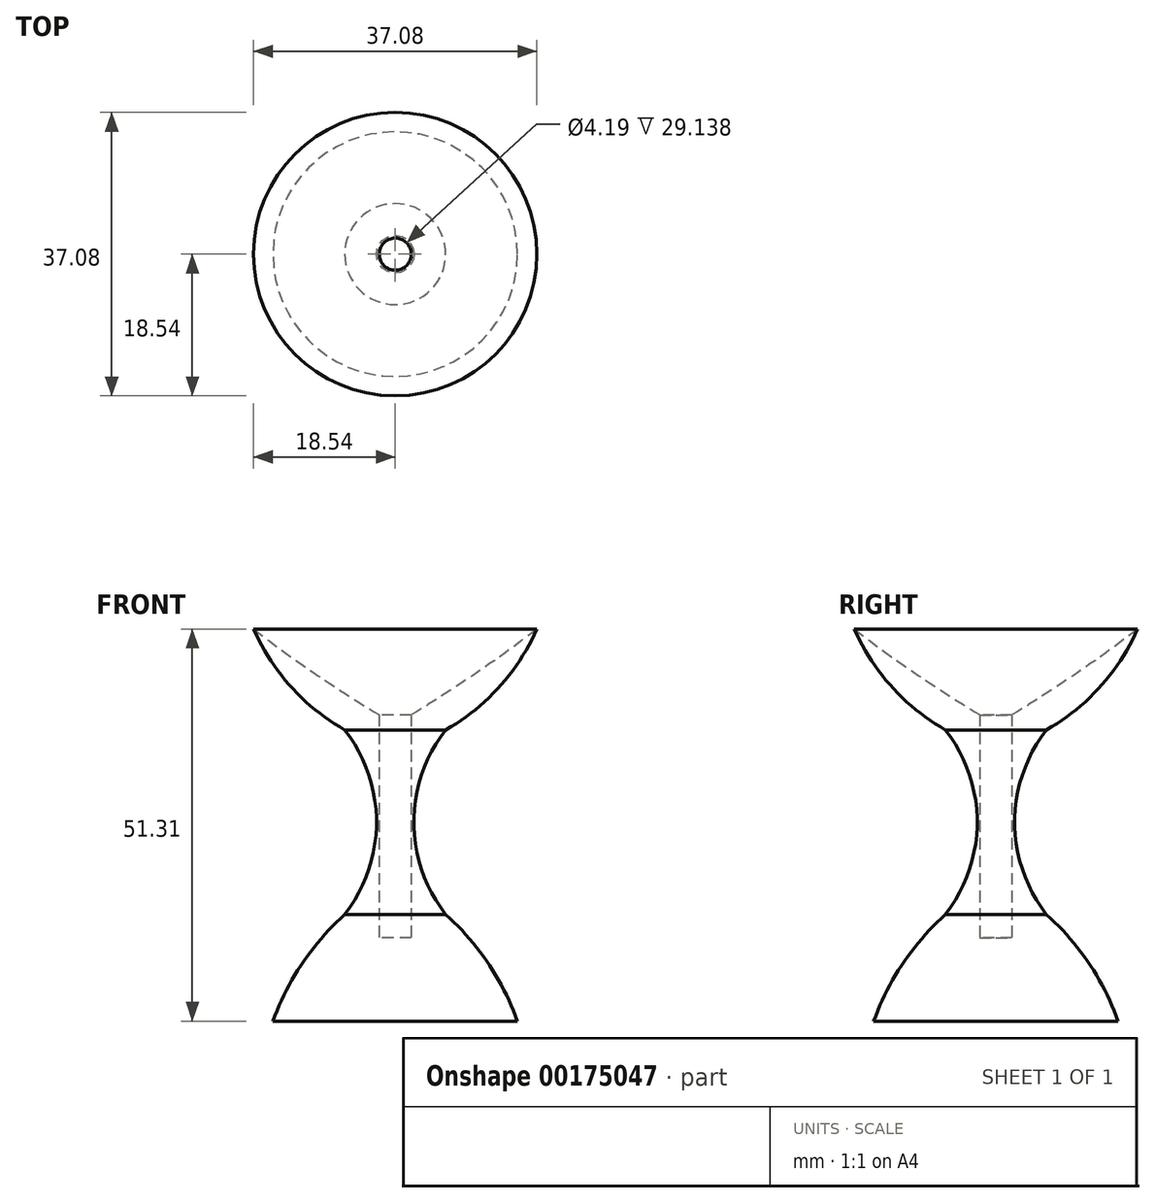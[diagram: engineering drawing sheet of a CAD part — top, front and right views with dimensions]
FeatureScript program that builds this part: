
annotation { "Feature Type Name" : "Feature", "Feature Type Description" : "" }
export const myFeature = defineFeature(function(context is Context, id is Id, definition is map)
    precondition{}
    {
        {
            var Q0;
            Q0=qCreatedBy(makeId("Front.planeOp"),FACE);
            var sketch = newSketch(context, id + "F0", { "sketchPlane" : qUnion([Q0])});
            skLineSegment(sketch, "E0", {"start": v(0, 53.09) * mm, "end": v(0, -54.61) * mm});
            skArc(sketch, "E1", {"start": v(-18.54, 40.39) * mm, "mid": v(-13.64, 32.82) * mm, "end": v(-6.6, 27.18) * mm});
            skArc(sketch, "E2", {"start": v(-6.6, 3.05) * mm, "mid": v(-2.46, 15.11) * mm, "end": v(-6.6, 27.18) * mm});
            skArc(sketch, "E3", {"start": v(-6.6, 3.05) * mm, "mid": v(-12.16, -3.36) * mm, "end": v(-16, -10.92) * mm});
            skLineSegment(sketch, "E4", {"start": v(-16, -10.92) * mm, "end": v(0, -10.92) * mm});
            skArc(sketch, "E5", {"start": v(-18.54, 40.39) * mm, "mid": v(-9.47, 33.85) * mm, "end": v(0, 27.89) * mm});
            skSolve(sketch);
        }
        {
            var Q0;
            Q0 = qSketchRegion(id + "F0", true);
            var Q1;
            Q1=sQuery(id+"F0.wireOp",EDGE,"E0");
            revolve(context, id + "F1", {"entities" : qUnion([Q0]), "axis" : qUnion([Q1]), "revolveType" : RevolveType.FULL});
        }
        {
            var Q0;
            Q0=qCreatedBy(makeId("Top.planeOp"),FACE);
            var sketch = newSketch(context, id + "F2", { "sketchPlane" : qUnion([Q0])});
            skCircle(sketch, "E6", {"center": v(0, 0) * mm, "radius": 2.1 * mm});
            skSolve(sketch);
        }
        {
            var Q0;
            Q0 = qSketchRegion(id + "F2", true);
            extrude(context, id + "F3", {"entities" : qUnion([Q0]), "operationType" : NewBodyOperationType.REMOVE, "depth" : 381 * mm, "offsetDistance" : 25.4 * mm});
        }
    });
